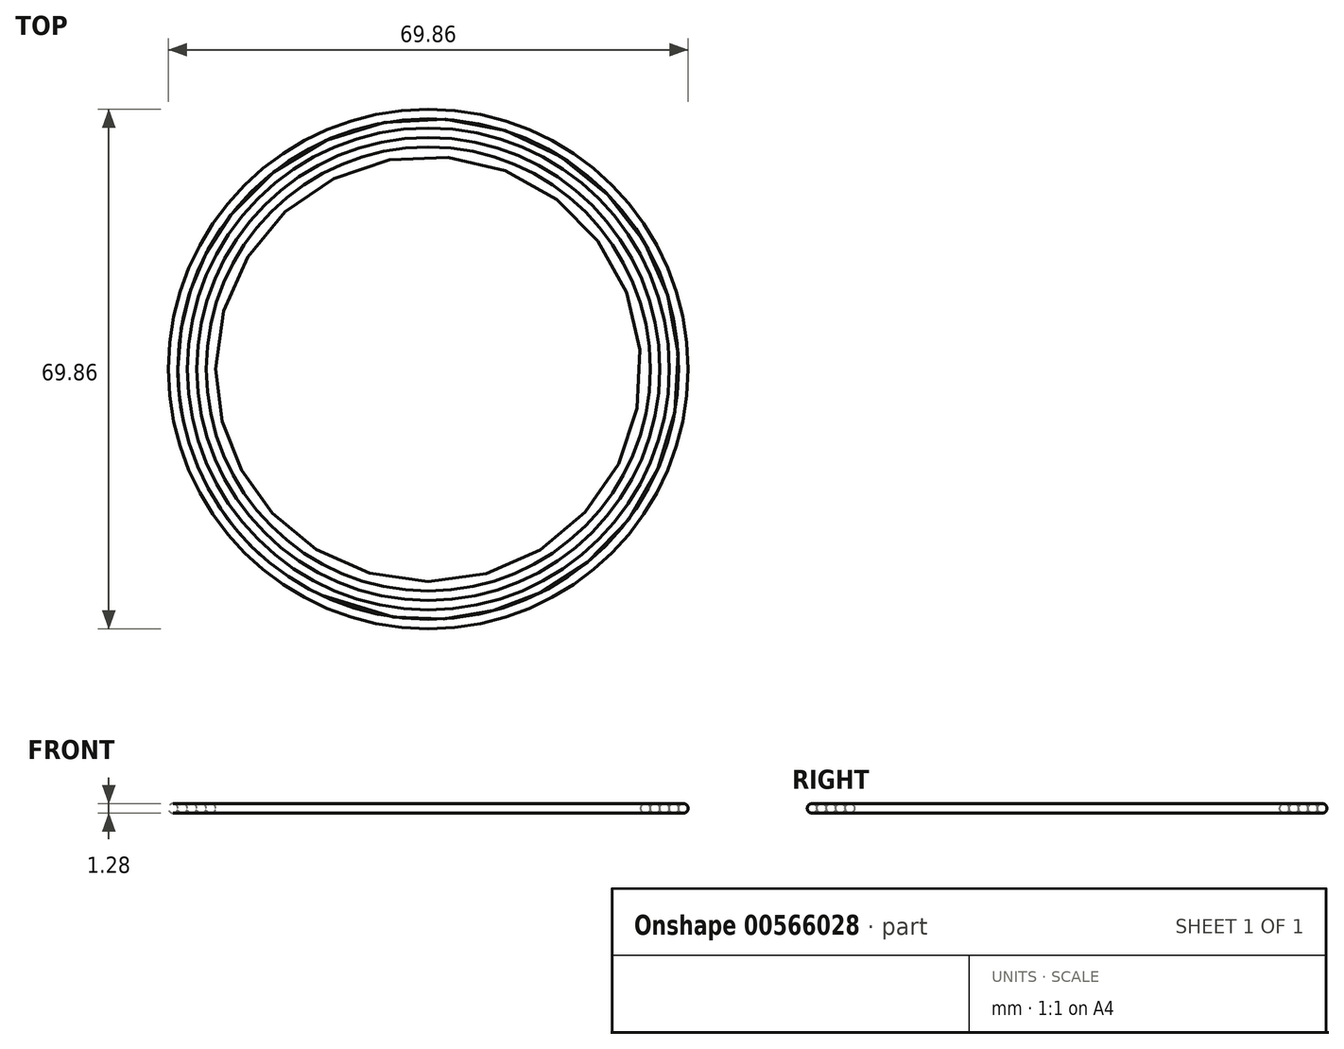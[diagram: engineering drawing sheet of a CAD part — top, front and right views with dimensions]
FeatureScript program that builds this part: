
annotation { "Feature Type Name" : "Feature", "Feature Type Description" : "" }
export const myFeature = defineFeature(function(context is Context, id is Id, definition is map)
    precondition{}
    {
        {
            var Q0;
            Q0=qCreatedBy(makeId("Right.planeOp"),FACE);
            var sketch = newSketch(context, id + "F0", { "sketchPlane" : qUnion([Q0])});
            skCircle(sketch, "E0", {"center": v(29.21, 0) * mm, "radius": 0.64 * mm});
            skLineSegment(sketch, "E1", {"start": v(0, 0) * mm, "end": v(0, 1.38) * mm, "construction": true});
            skCircle(sketch, "E2.1.0.0", {"center": v(30.48, 0) * mm, "radius": 0.64 * mm});
            skCircle(sketch, "E2.2.0.0", {"center": v(31.75, 0) * mm, "radius": 0.64 * mm});
            skCircle(sketch, "E2.3.0.0", {"center": v(33.02, 0) * mm, "radius": 0.64 * mm});
            skCircle(sketch, "E2.4.0.0", {"center": v(34.3, 0) * mm, "radius": 0.64 * mm});
            skLineSegment(sketch, "E2.direction1", {"start": v(29.21, 0) * mm, "end": v(30.48, 0) * mm, "construction": true});
            skSolve(sketch);
        }
        {
            var Q0;
            Q0 = qSketchRegion(id + "F0", true);
            var Q1;
            Q1=sQuery(id+"F0.wireOp",EDGE,"E1");
            revolve(context, id + "F1", {"entities" : qUnion([Q0]), "axis" : qUnion([Q1]), "revolveType" : RevolveType.FULL});
        }
    });
